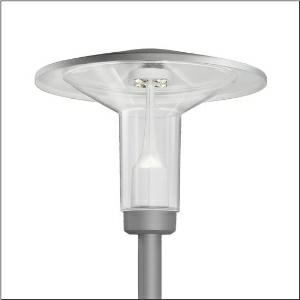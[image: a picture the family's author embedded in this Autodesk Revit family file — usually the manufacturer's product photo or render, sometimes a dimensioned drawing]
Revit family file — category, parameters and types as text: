
# Revit family: laterne_iq___st1_2a_5xa5255ef14h_6af0
name_source: partatom
category: Lighting Fixtures
units: mm (PartAtom-declared; Revit-internal decimal feet)

## family parameters
Cut with Voids When Loaded = No
Host = Face
Light Source = No
Part Type = Normal
Room Calculation Point = No
Round Connector Dimension = Use Diameter
Shared = No

## types (1)
- --- (1 x LED, 1540 lm, 10.5 W, 3000K)
    Apparent Load = 11 VA
    CIE Flux Codes = 25 63 94 98 100
    Color Rendering = 70
    Color Temperature = 3000K
    Default Elevation = 1800 mm
    Description = Lantern iQ, mast luminaire, Module 540 iQ-SR, primary light control with 3 zone facetted reflector, of plastic, silver coated, highly specular, structured, primary optical cover: cover, of PMMA, transparent, light distribution: ST1.2a, light emission: direct distribution, primary light characteristic: asymmetric, installation type: post-top, LED, High Power LED, rated luminous flux: 1.540lm, luminous efficacy: 147lm/W, light colour: 730, colour temperature: 3000K, control gear: iQ Street-Remote, control: Auto-Match, Temp-Guard, Lumen-Switch, Night-Set, Smart-Wire, Light-Fading, Desk-Remote (wireless, voltage-free reading and setting of iQ features in the workshop via application-optimized NFC function/RFID function), optimised constant luminous flux control (CLO 2.0), Street-Remote, pre-setting: logarithmic dimming characteristic, with terminal, 6-pole, max. 2.5mm², mains connection: 230..240V, AC, 50/60Hz, start of lifetime: 11W, end of service life: 11W, reduction: 5W, luminaire housing, upper part, of glass-fibre reinforced polyester, coated, Siteco® metallic grey (DB 702S), diameter: 750mm, height: 583mm, spigot size: d x l = 76 x 70mm (post-top) | with reducer (optional accessory) 60 x 70mm, mounting height: 3..5m, post-top mast mounting element, of diecast aluminium, coated, Siteco® metallic grey (DB 702S), Module 540 iQ-SR, traffic white (RAL 9016), equipment: standard, protection rating (complete): IP65, insulation class (complete): insulation class II (safety insulation), certification: CE, ENEC, VDE, packaging unit: 1 piece

Light Distribution: ST1.2a
    Height = 583 mm
    Lamp = 1 x LED
    Lamp Light Flux = 1540 lm
    Lamp Power = 10.5 W
    Lamp count = 1
    Length = 750 mm
    Luminous efficacy = 147 lm/W
    Manufacturer = Siteco
    ModVariant = No
    Model = 5XA5255EF14H
    Number of Poles = 1
    OnlyDefault = Yes
    Power Factor = 1
    Product Name = Laterne iQ | ST1.2a
    Product group = mast luminaire | pylon top
    ProductGroupID = 6100
    Protection Class = Protection class II
    Protection Degree = IP 65
    RLX_Detail_Level = 1
    RLX_Emergency_Light_Flux = 0 lm
    RLX_Emergency_Type = 0
    RLX_Emergency_Type_DB = No
    RlxData = <blob elided: 88553 chars, md5=035344ff>
    Socket = socket
    Standby Power = 0 W
    System Light Flux = 1540 lm
    System Power = 11 W
    Type Comments = factory setting: luminous flux: 100 % | dim-lin: 254 | 419 mA
    Type Image = l_1006050.jpg
    URL = http://relux.com
    VarID = @adj_160660
    Voltage = 0 V
    Weight = 0.00 kg
    Width = 0 mm  [stored 0 ft]

note: [stored X ft] marks values corroborated as IEEE doubles in the binary element streams (Revit-internal decimal feet)

## geometry (parser evidence)
native form markers: Blend x4, Sweep x11
no freeform markers — native parametric forms only
